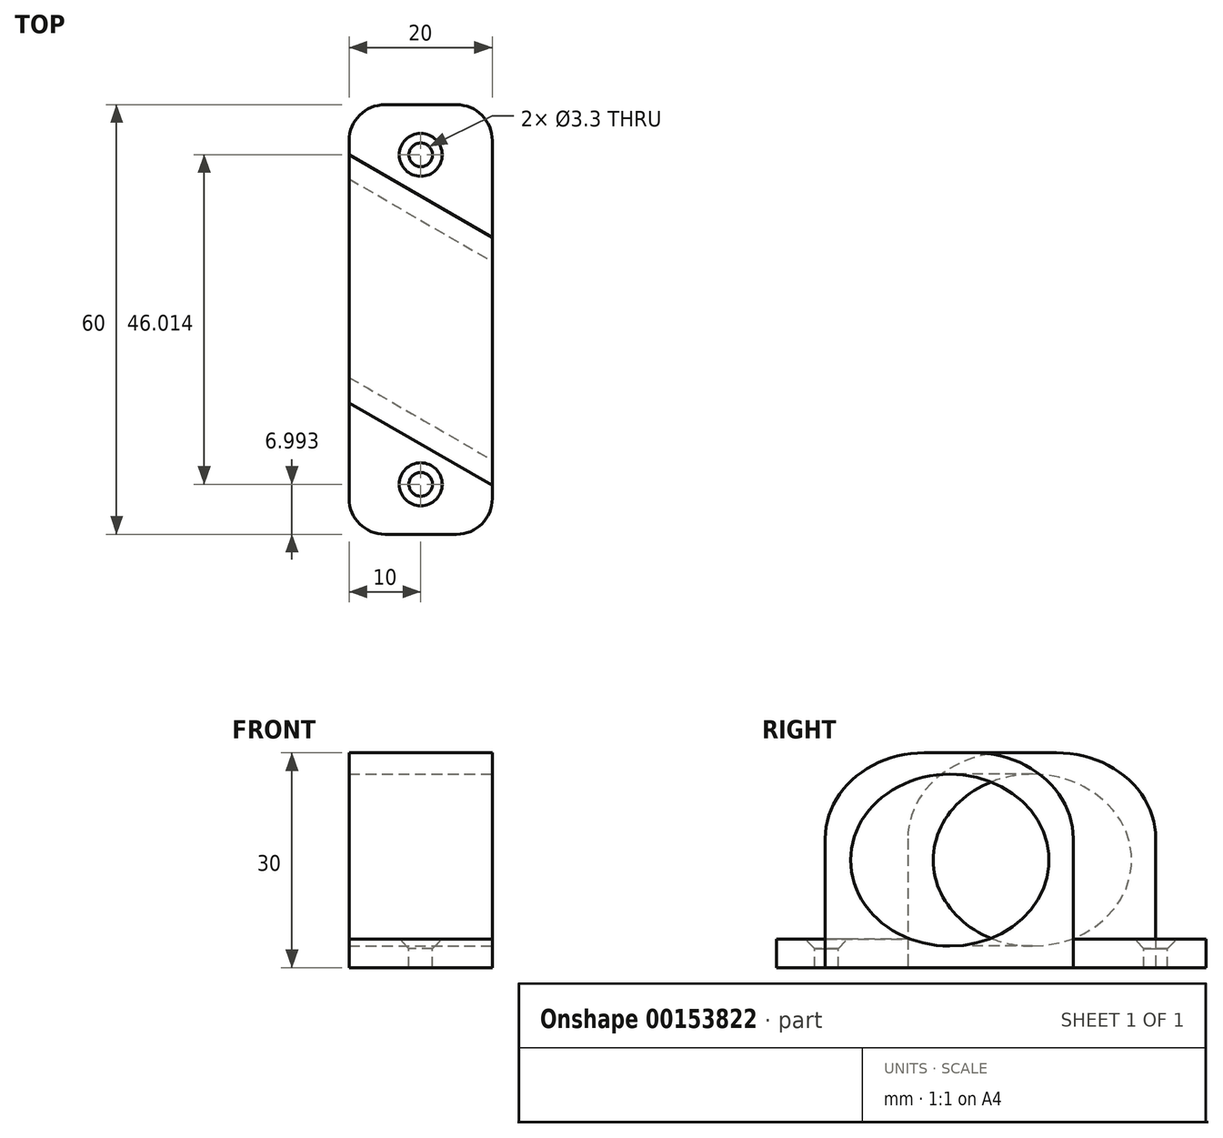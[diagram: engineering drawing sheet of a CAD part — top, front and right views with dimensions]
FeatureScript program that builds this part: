
annotation { "Feature Type Name" : "Feature", "Feature Type Description" : "" }
export const myFeature = defineFeature(function(context is Context, id is Id, definition is map)
    precondition{}
    {
        {
            var Q0;
            Q0=qCreatedBy(makeId("Top.planeOp"),FACE);
            var sketch = newSketch(context, id + "F0", { "sketchPlane" : qUnion([Q0])});
            skLineSegment(sketch, "E0.bottom", {"start": v(-10, 30) * mm, "end": v(10, 30) * mm});
            skLineSegment(sketch, "E0.top", {"start": v(-10, -30) * mm, "end": v(10, -30) * mm});
            skLineSegment(sketch, "E0.left", {"start": v(-10, 30) * mm, "end": v(-10, -30) * mm});
            skLineSegment(sketch, "E0.right", {"start": v(10, 30) * mm, "end": v(10, -30) * mm});
            skPoint(sketch, "E0.middle", {"position": v(0, 0) * mm});
            skLineSegment(sketch, "E1", {"start": v(-10, 23) * mm, "end": v(10, 11.46) * mm});
            skLineSegment(sketch, "E2", {"start": v(10, -23.18) * mm, "end": v(-10, -11.63) * mm});
            skPoint(sketch, "E3.orphan", {"position": v(29.85, 0) * mm});
            skPoint(sketch, "E4.orphan", {"position": v(29.85, -34.64) * mm});
            skSolve(sketch);
        }
        {
            var Q0;
            {var subQ0=sQuery(id+"F0.wireOp",EDGE,"E0.bottom");Q0=makeQuery(id+"F0.imprint","IMPRINT",FACE,{"disambiguationData":[TD([[makeQuery(id+"F0.imprint","IMPRINT",EDGE,{"derivedFrom":subQ0}),-1.0]])]});}
            var Q1;
            {var subQ0=sQuery(id+"F0.wireOp",EDGE,"E0.top");Q1=makeQuery(id+"F0.imprint","IMPRINT",FACE,{"disambiguationData":[TD([[makeQuery(id+"F0.imprint","IMPRINT",EDGE,{"derivedFrom":subQ0}),1.0]])]});}
            extrude(context, id + "F1", {"entities" : qUnion([Q0, Q1]), "depth" : 4 * mm});
        }
        {
            var Q0;
            {var subQ0=sQuery(id+"F0.wireOp",EDGE,"E1");Q0=makeQuery(id+"F0.imprint","IMPRINT",FACE,{"disambiguationData":[TD([[makeQuery(id+"F0.imprint","IMPRINT",EDGE,{"derivedFrom":subQ0}),-1.0]])]});}
            extrude(context, id + "F2", {"entities" : qUnion([Q0]), "depth" : 30 * mm});
        }
        {
            var Q0;
            Q0=makeQuery(id+"F2.opExtrude","SWEPT_FACE",FACE,{"disambiguationData":[OSD([sQuery(id+"F0.wireOp",EDGE,"E1")])]});
            var sketch = newSketch(context, id + "F3", { "sketchPlane" : qUnion([Q0])});
            skLineSegment(sketch, "E5.bottom", {"start": v(-2.93, 15.59) * mm, "end": v(15.1, 15.59) * mm});
            skLineSegment(sketch, "E5.top", {"start": v(-2.93, 27.37) * mm, "end": v(15.1, 27.37) * mm});
            skLineSegment(sketch, "E5.left", {"start": v(-2.93, 15.59) * mm, "end": v(-2.93, 27.37) * mm});
            skLineSegment(sketch, "E5.right", {"start": v(15.1, 15.59) * mm, "end": v(15.1, 27.37) * mm});
            skPoint(sketch, "E5.middle", {"position": v(6.09, 21.48) * mm});
            skSolve(sketch);
        }
        {
            var Q0;
            Q0=makeQuery(id+"F3.imprint","IMPRINT",FACE,{"disambiguationData":[TD([[makeQuery(id+"F3.imprint","IMPRINT",EDGE,{"derivedFrom":sQuery(id+"F3.wireOp",EDGE,"E5.bottom")}),1.0]])]});
            extrude(context, id + "F4", {"entities" : qUnion([Q0]), "operationType" : NewBodyOperationType.ADD, "depth" : 25 * mm});
        }
        {
            var Q0;
            Q0=makeQuery(id+"F4.opExtrude","SWEPT_FACE",FACE,{"disambiguationData":[OSD([sQuery(id+"F3.wireOp",EDGE,"E5.left")])]});
            cPlane(context, id + "F5", {"entities" : qUnion([Q0]), "cplaneType" : CPlaneType.OFFSET, "offset" : 0 * mm, "width" : 150 * mm, "height" : 150 * mm});
        }
        {
            var Q0;
            Q0=qCreatedBy(id+"F5.planeOp",FACE);
            var sketch = newSketch(context, id + "F6", { "sketchPlane" : qUnion([Q0])});
            skLineSegment(sketch, "E6", {"start": v(0, 0) * mm, "end": v(0, 30) * mm, "construction": true});
            skLineSegment(sketch, "E7.0", {"start": v(14.92, 30) * mm, "end": v(-15.08, 30) * mm});
            skPoint(sketch, "E8", {"position": v(0, 15) * mm});
            skCircle(sketch, "E9", {"center": v(0, 15) * mm, "radius": 12 * mm});
            skSolve(sketch);
        }
        {
            var Q0;
            Q0 = qSketchRegion(id + "F6", true);
            extrude(context, id + "F7", {"entities" : qUnion([Q0]), "operationType" : NewBodyOperationType.REMOVE, "oppositeDirection" : true, "depth" : 25 * mm, "hasSecondDirection" : true, "secondDirectionOppositeDirection" : false, "secondDirectionDepth" : 25 * mm});
        }
        {
            var Q0;
            Q0=makeQuery(id+"F4.opExtrude","SWEPT_FACE",FACE,{"disambiguationData":[OSD([sQuery(id+"F3.wireOp",EDGE,"E5.left")])]});
            extrude(context, id + "F8", {"entities" : qUnion([Q0]), "operationType" : NewBodyOperationType.REMOVE, "oppositeDirection" : true, "depth" : 25 * mm});
        }
        {
            var Q0;
            Q0=makeQuery(id+"F1.opExtrude","CAP_FACE",FACE,{"disambiguationData":[OSD([sQuery(id+"F0.wireOp",EDGE,"E0.bottom"),sQuery(id+"F0.wireOp",EDGE,"E0.left"),sQuery(id+"F0.wireOp",EDGE,"E0.right"),sQuery(id+"F0.wireOp",EDGE,"E1")])],"isStart":false});
            var sketch = newSketch(context, id + "F9", { "sketchPlane" : qUnion([Q0])});
            skLineSegment(sketch, "E10", {"start": v(-10, 23) * mm, "end": v(10, 23) * mm, "construction": true});
            skPoint(sketch, "E11", {"position": v(0, 23) * mm});
            skPoint(sketch, "E12.MirrorP", {"position": v(0, -23) * mm});
            skSolve(sketch);
        }
        {
            var Q0;
            Q0=sQuery(id+"F9.wireOp",VERTEX,"E11");
            var Q1;
            Q1=sQuery(id+"F9.wireOp",VERTEX,"E12.MirrorP");
            var Q2;
            Q2=makeQuery(id+"F1.opExtrude","SWEPT_BODY",BODY,{"disambiguationData":[OSD([sQuery(id+"F0.wireOp",EDGE,"E0.bottom"),sQuery(id+"F0.wireOp",EDGE,"E0.left"),sQuery(id+"F0.wireOp",EDGE,"E0.right"),sQuery(id+"F0.wireOp",EDGE,"E1")])]});
            var Q3;
            Q3=makeQuery(id+"F1.opExtrude","SWEPT_BODY",BODY,{"disambiguationData":[OSD([sQuery(id+"F0.wireOp",EDGE,"E0.top"),sQuery(id+"F0.wireOp",EDGE,"E0.left"),sQuery(id+"F0.wireOp",EDGE,"E0.right"),sQuery(id+"F0.wireOp",EDGE,"E2")])]});
            hole(context, id + "F10", {"style" : HoleStyle.C_SINK, "endStyle" : HoleEndStyle.THROUGH, "holeDiameter" : 3.3 * mm, "cSinkDiameter" : 6 * mm, "cSinkAngle" : 90 * degree, "locations" : qUnion([Q0, Q1]), "scope" : qUnion([Q2, Q3]), "isTappedThrough" : true});
        }
        {
            var Q0;
            Q0=makeQuery(id+"F1.opExtrude","SWEPT_EDGE",EDGE,{"disambiguationData":[OSD([sQuery(id+"F0.wireOp",EDGE,"E0.bottom"),sQuery(id+"F0.wireOp",EDGE,"E0.right")])]});
            var Q1;
            Q1=makeQuery(id+"F1.opExtrude","SWEPT_EDGE",EDGE,{"disambiguationData":[OSD([sQuery(id+"F0.wireOp",EDGE,"E0.bottom"),sQuery(id+"F0.wireOp",EDGE,"E0.left")])]});
            var Q2;
            Q2=makeQuery(id+"F1.opExtrude","SWEPT_EDGE",EDGE,{"disambiguationData":[OSD([sQuery(id+"F0.wireOp",EDGE,"E0.top"),sQuery(id+"F0.wireOp",EDGE,"E0.left")])]});
            var Q3;
            Q3=makeQuery(id+"F1.opExtrude","SWEPT_EDGE",EDGE,{"disambiguationData":[OSD([sQuery(id+"F0.wireOp",EDGE,"E0.top"),sQuery(id+"F0.wireOp",EDGE,"E0.right")])]});
            fillet(context, id + "F11", {"entities" : qUnion([Q0, Q1, Q2, Q3]), "radius" : 5 * mm, "tangentPropagation" : true, "allowEdgeOverflow" : false});
        }
        {
            var Q0;
            Q0=makeQuery(id+"F2.opExtrude","CAP_EDGE",EDGE,{"disambiguationData":[OSD([sQuery(id+"F0.wireOp",EDGE,"E2")])],"isStart":false});
            var Q1;
            Q1=makeQuery(id+"F2.opExtrude","CAP_EDGE",EDGE,{"disambiguationData":[OSD([sQuery(id+"F0.wireOp",EDGE,"E1")])],"isStart":false});
            fillet(context, id + "F12", {"entities" : qUnion([Q0, Q1]), "radius" : 12 * mm, "tangentPropagation" : true, "allowEdgeOverflow" : false});
        }
    });
